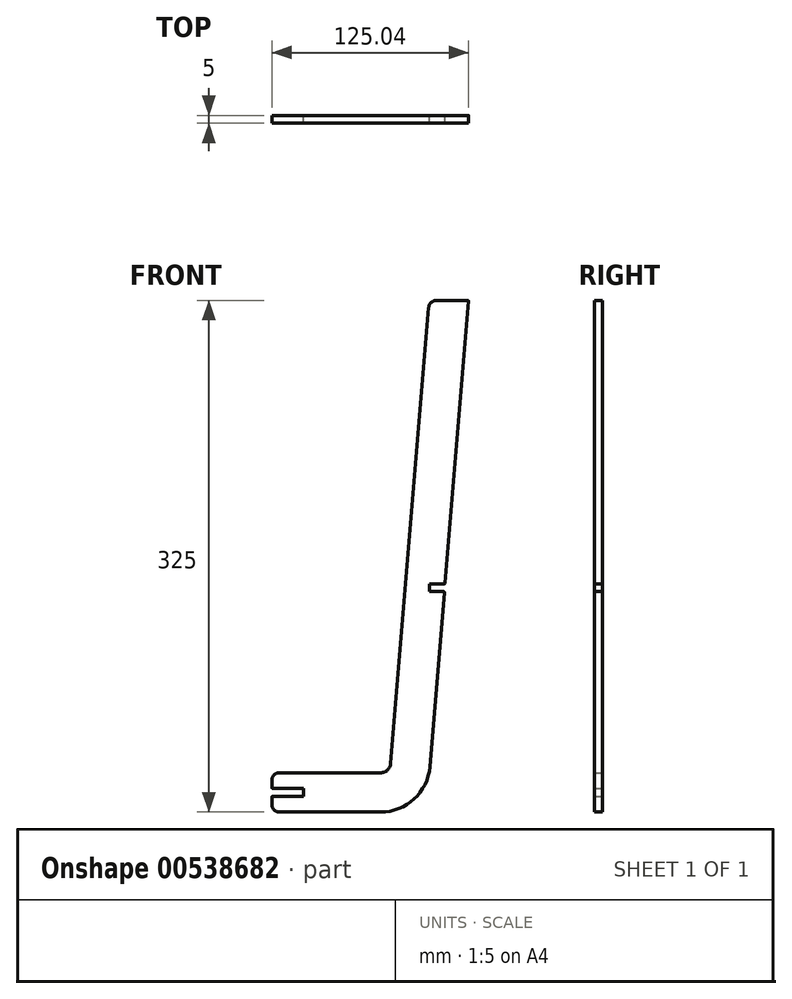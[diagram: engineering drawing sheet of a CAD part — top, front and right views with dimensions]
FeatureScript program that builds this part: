
annotation { "Feature Type Name" : "Feature", "Feature Type Description" : "" }
export const myFeature = defineFeature(function(context is Context, id is Id, definition is map)
    precondition{}
    {
        {
            var Q0;
            Q0=qCreatedBy(makeId("Front.planeOp"),FACE);
            var sketch = newSketch(context, id + "F0", { "sketchPlane" : qUnion([Q0])});
            skLineSegment(sketch, "E0.bottom", {"start": v(75, 150) * mm, "end": v(-75, 150) * mm, "construction": true});
            skLineSegment(sketch, "E0.top", {"start": v(75, -150) * mm, "end": v(-75, -150) * mm, "construction": true});
            skLineSegment(sketch, "E0.left", {"start": v(75, 150) * mm, "end": v(75, -150) * mm, "construction": true});
            skLineSegment(sketch, "E0.right", {"start": v(-75, 150) * mm, "end": v(-75, -150) * mm, "construction": true});
            skPoint(sketch, "E0.middle", {"position": v(0, 0) * mm});
            skLineSegment(sketch, "E1", {"start": v(24.62, 145.42) * mm, "end": v(0.49, -144.18) * mm});
            skLineSegment(sketch, "E2", {"start": v(-5.84, -150) * mm, "end": v(-70, -150) * mm});
            skPoint(sketch, "E3.visualSharp", {"position": v(0, -150) * mm});
            skArc(sketch, "E3.filletArc", {"start": v(-5.84, -150) * mm, "mid": v(-1.54, -148.32) * mm, "end": v(0.49, -144.18) * mm});
            skLineSegment(sketch, "E4.0", {"start": v(-5.84, -175) * mm, "end": v(-70, -175) * mm});
            skArc(sketch, "E4.1", {"start": v(-5.84, -175) * mm, "mid": v(15.38, -166.72) * mm, "end": v(25.4, -146.25) * mm});
            skLineSegment(sketch, "E4.2", {"start": v(50.04, 149.46) * mm, "end": v(35.09, -30) * mm});
            skLineSegment(sketch, "E5", {"start": v(-75, -155) * mm, "end": v(-75, -170) * mm, "construction": true});
            skLineSegment(sketch, "E6", {"start": v(49.54, 150) * mm, "end": v(29.6, 150) * mm});
            skPoint(sketch, "E7.visualSharp", {"position": v(50.09, 150) * mm});
            skArc(sketch, "E7.filletArc", {"start": v(50.04, 149.46) * mm, "mid": v(49.91, 149.84) * mm, "end": v(49.54, 150) * mm});
            skPoint(sketch, "E8.visualSharp", {"position": v(25, 150) * mm});
            skArc(sketch, "E8.filletArc", {"start": v(29.6, 150) * mm, "mid": v(26.22, 148.68) * mm, "end": v(24.62, 145.42) * mm});
            skPoint(sketch, "E9.visualSharp", {"position": v(-75, -150) * mm});
            skArc(sketch, "E9.filletArc", {"start": v(-70, -150) * mm, "mid": v(-73.54, -151.46) * mm, "end": v(-75, -155) * mm});
            skPoint(sketch, "E10.visualSharp", {"position": v(-75, -175) * mm});
            skArc(sketch, "E10.filletArc", {"start": v(-75, -170) * mm, "mid": v(-73.54, -173.54) * mm, "end": v(-70, -175) * mm});
            skLineSegment(sketch, "E11", {"start": v(-75, -162.5) * mm, "end": v(46.34, -162.5) * mm, "construction": true});
            skLineSegment(sketch, "E12", {"start": v(-75, -155) * mm, "end": v(-75, -160.02) * mm, "construction": true});
            skLineSegment(sketch, "E13", {"start": v(-75, -160.02) * mm, "end": v(-55, -160.02) * mm, "construction": true});
            skLineSegment(sketch, "E14", {"start": v(-55, -160.02) * mm, "end": v(-55, -164.97) * mm, "construction": true});
            skLineSegment(sketch, "E15", {"start": v(-55, -164.98) * mm, "end": v(-75, -164.98) * mm, "construction": true});
            skLineSegment(sketch, "E16", {"start": v(-75, -164.98) * mm, "end": v(-75, -170) * mm, "construction": true});
            skLineSegment(sketch, "E17", {"start": v(-75, -155) * mm, "end": v(-75, -160.02) * mm});
            skLineSegment(sketch, "E18", {"start": v(-55, -160.02) * mm, "end": v(-55, -164.97) * mm});
            skLineSegment(sketch, "E19", {"start": v(-75, -164.98) * mm, "end": v(-75, -170) * mm});
            skLineSegment(sketch, "E20", {"start": v(-75, -160.02) * mm, "end": v(-55, -160.02) * mm});
            skLineSegment(sketch, "E21", {"start": v(-75, -164.97) * mm, "end": v(-55, -164.97) * mm});
            skLineSegment(sketch, "E22", {"start": v(34.67, -34.95) * mm, "end": v(25.09, -34.95) * mm});
            skLineSegment(sketch, "E23", {"start": v(25.09, -34.95) * mm, "end": v(25.09, -30) * mm, "construction": true});
            skLineSegment(sketch, "E24", {"start": v(25.09, -30) * mm, "end": v(35.09, -30) * mm});
            skLineSegment(sketch, "E25", {"start": v(25.09, -34.95) * mm, "end": v(25.09, -30) * mm});
            skLineSegment(sketch, "E26.trimOffspring", {"start": v(34.67, -34.95) * mm, "end": v(25.4, -146.25) * mm});
            skSolve(sketch);
        }
        {
            var Q0;
            Q0=makeQuery(id+"F0.imprint","IMPRINT",FACE,{"disambiguationData":[TD([[makeQuery(id+"F0.imprint","IMPRINT",EDGE,{"derivedFrom":sQuery(id+"F0.wireOp",EDGE,"E1")}),1.0]])]});
            extrude(context, id + "F1", {"entities" : qUnion([Q0]), "depth" : 5 * mm, "offsetDistance" : 25.4 * mm});
        }
        {
            var Q0;
            Q0=makeQuery(id+"F1.opExtrude","SWEPT_EDGE",EDGE,{"disambiguationData":[OSD([sQuery(id+"F0.wireOp",EDGE,"E4.2"),sQuery(id+"F0.wireOp",EDGE,"E24")])]});
            fillet(context, id + "F2", {"entities" : qUnion([Q0]), "radius" : .5 * mm, "tangentPropagation" : true, "allowEdgeOverflow" : false});
        }
        {
            var Q0;
            Q0=makeQuery(id+"F1.opExtrude","SWEPT_EDGE",EDGE,{"disambiguationData":[OSD([sQuery(id+"F0.wireOp",EDGE,"E22"),sQuery(id+"F0.wireOp",EDGE,"E26.trimOffspring")])]});
            fillet(context, id + "F3", {"entities" : qUnion([Q0]), "radius" : .5 * mm, "tangentPropagation" : true, "allowEdgeOverflow" : false});
        }
        {
            var Q0;
            Q0=makeQuery(id+"F1.opExtrude","SWEPT_EDGE",EDGE,{"disambiguationData":[OSD([sQuery(id+"F0.wireOp",EDGE,"E19"),sQuery(id+"F0.wireOp",EDGE,"E21")])]});
            var Q1;
            Q1=makeQuery(id+"F1.opExtrude","SWEPT_EDGE",EDGE,{"disambiguationData":[OSD([sQuery(id+"F0.wireOp",EDGE,"E17"),sQuery(id+"F0.wireOp",EDGE,"E20")])]});
            fillet(context, id + "F4", {"entities" : qUnion([Q0, Q1]), "radius" : .5 * mm, "tangentPropagation" : true, "allowEdgeOverflow" : false});
        }
    });
